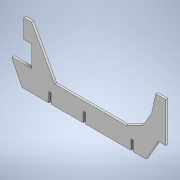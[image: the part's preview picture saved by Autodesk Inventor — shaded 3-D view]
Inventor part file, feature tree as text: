
AUTODESK INVENTOR PART (.ipt)
format: ipt  version: 2020 (Build 240168000, 168)  size: 135,680 bytes
history: native  units: mm
features: other x2, extrude x1
ambient origin geometry x8: Origin, YZ Plane, XZ Plane, XY Plane, X Axis, Y Axis, Z Axis, Center Point
bodies: Body1 (feature_tree)
feature tree (3):
  other  "Твердое тело1"
  extrude  "Выдавливание1"  Depth=8.0mm TaperAngle=0.0deg
  other  "Видимый контур (ГОСТ)"
